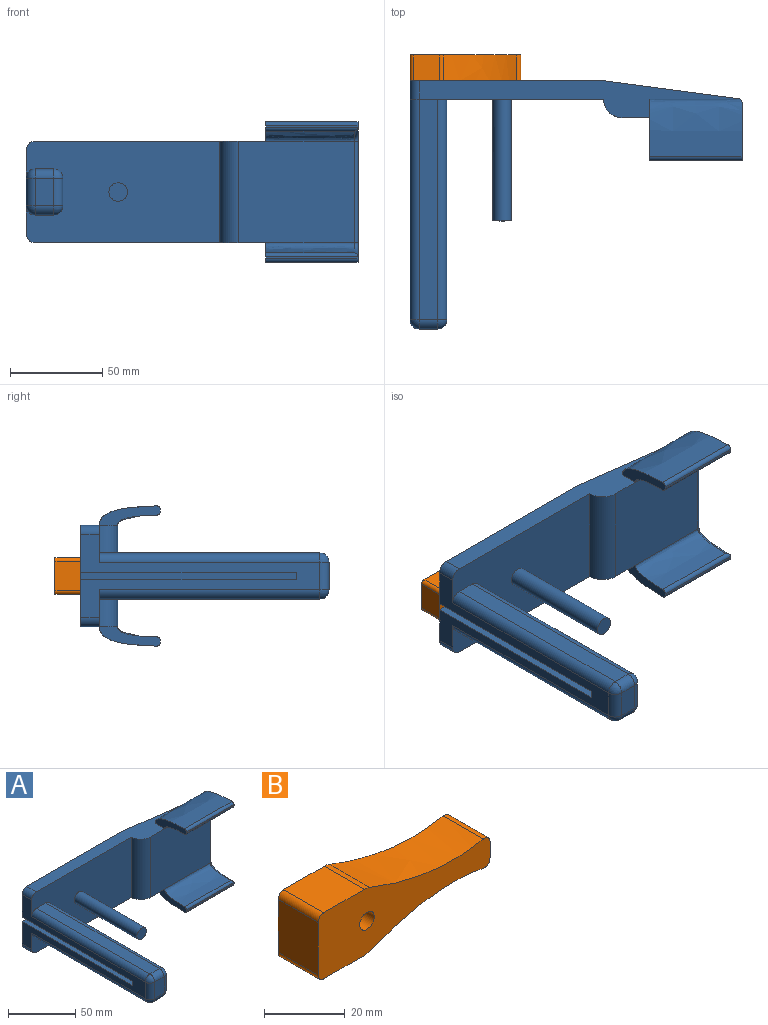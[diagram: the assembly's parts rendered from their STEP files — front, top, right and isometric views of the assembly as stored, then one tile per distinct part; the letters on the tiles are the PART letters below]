
ASSEMBLY  parts=2 mates=1
PART A: 53 faces, bbox 180x139.6x76.1 mm
  f0: plane 173.94x20mm, normal (0,0,1), area 1603.2mm2, adj f3,f15,f19,f21,f26,f28,f30,f32
  f1: plane 119.58x9.96mm, normal (0,0,-1), area 1191mm2, adj f15,f35,f40,f41
  f2: plane 119.58x9.96mm, normal (0,0,1), area 1191mm2, adj f15,f33,f38,f39
  f3: plane 104.98x55mm, normal (0,1,0), area 5710.5mm2, adj f0,f5,f7,f9,f10,f11,f12,f13
  f4: plane 119.58x15mm, normal (1,0,0), area 1793.7mm2, adj f15,f33,f34,f35
  f5: plane 129.58x45mm, normal (-1,0,0), area 1776.5mm2, adj f3,f9,f13,f14,f15,f31,f32,f38
  f6: plane 15x9.96mm, normal (0,-1,0), area 149.4mm2, adj f34,f39,f40,f44
  f7: cylinder r=2.5mm len=5mm, axis (0,-1,0), area 78.5mm2, adj f3,f8
  f8: plane 5x5mm, normal (0,1,0), area 19.6mm2, adj f7
  f9: plane 116.8x5mm, normal (0,0,-1), area 584mm2, adj f3,f5,f10,f14
  f10: plane 116.8x2.12mm, normal (0.71,0,-0.71), area 350.4mm2, adj f3,f9,f11,f14
  f11: plane 116.8x8.24mm, normal (-1,0,0), area 962.7mm2, adj f3,f10,f12,f14
  f12: plane 116.8x2.12mm, normal (0.71,0,0.71), area 350.4mm2, adj f3,f11,f13,f14
  f13: plane 116.8x5mm, normal (0,0,1), area 584mm2, adj f3,f5,f12,f14
  f14: plane 8.24x7.12mm, normal (0,1,0), area 33mm2, adj f5,f9,f10,f11,f12,f13
  f15: plane 104.98x55mm, normal (0,-1,0), area 5207mm2, adj f0,f1,f2,f4,f5,f16,f18,f30
  f16: cylinder r=5mm len=66mm, axis (0,1,0), area 2073.5mm2, adj f15,f17
  f17: plane 10x10mm, normal (0,-1,0), area 78.5mm2, adj f16
  f18: plane 173.94x20mm, normal (0,0,-1), area 1603.2mm2, adj f3,f15,f19,f21,f23,f24,f30,f31
  f19: plane 63x55mm, normal (0,-1,0), area 3465mm2, adj f0,f18,f25,f27,f30,f47
  f20: plane 76.06x33.12mm, normal (1,0,0), area 594.8mm2, adj f22,f24,f28,f29,f46,f47,f49,f50
  f21: plane 73.26x55mm, normal (0.13,0.99,0), area 4065.2mm2, adj f0,f3,f18,f52
  f22: plane 50x1.01mm, normal (0,-1,0), area 50.4mm2, adj f20,f23,f48,f49,f51
  f23: plane 33.11x10.53mm, normal (-1,0,0), area 183mm2, adj f18,f22,f24,f25,f48,f51
  f24: extruded ~50x31.09mm, area 1763.7mm2, adj f18,f20,f23,f51,f52
  f25: extruded ~48x21.14mm, area 1106.2mm2, adj f19,f23,f48,f49
  f26: plane 33.11x10.53mm, normal (-1,0,0), area 183mm2, adj f0,f27,f28,f29,f45,f50
  f27: extruded ~48x21.14mm, area 1106.2mm2, adj f19,f26,f45,f46
  f28: extruded ~50x31.09mm, area 1763.7mm2, adj f0,f20,f26,f50,f52
  f29: plane 50x1.01mm, normal (0,-1,0), area 50.4mm2, adj f20,f26,f45,f46,f50
  f30: cylinder r=10mm len=55mm, axis (0,0,-1), area 863.9mm2, adj f0,f15,f18,f19
  f31: cylinder r=5mm len=10mm, axis (0,-1,0), area 78.5mm2, adj f3,f5,f15,f18
  f32: cylinder r=5mm len=10mm, axis (0,-1,0), area 78.5mm2, adj f0,f3,f5,f15
  f33: cylinder r=5mm len=119.58mm, axis (0,-1,0), area 939.2mm2, adj f2,f4,f15,f36
  f34: cylinder r=5mm len=15mm, axis (0,0,1), area 117.8mm2, adj f4,f6,f36,f37
  f35: cylinder r=5mm len=119.58mm, axis (0,1,0), area 939.2mm2, adj f1,f4,f15,f37
  f36: sphere r=5mm, area 39.3mm2, adj f33,f34,f39
  f37: sphere r=5mm, area 39.3mm2, adj f34,f35,f40
  f38: cylinder r=5mm len=119.58mm, axis (0,1,0), area 939.2mm2, adj f2,f5,f15,f42
  f39: cylinder r=5mm len=9.96mm, axis (-1,0,0), area 78.2mm2, adj f2,f6,f36,f42
  f40: cylinder r=5mm len=9.96mm, axis (1,0,0), area 78.2mm2, adj f1,f6,f37,f43
  f41: cylinder r=5mm len=119.58mm, axis (0,-1,0), area 939.2mm2, adj f1,f5,f15,f43
  f42: sphere r=5mm, area 39.3mm2, adj f38,f39,f44
  f43: sphere r=5mm, area 39.3mm2, adj f40,f41,f44
  f44: cylinder r=5mm len=15mm, axis (0,0,-1), area 117.8mm2, adj f5,f6,f42,f43
  f45: cylinder r=2mm len=50mm, axis (1,0,0), area 152.5mm2, adj f26,f27,f29,f46
  f46: bspline ~26.24x10.11mm, area 79.9mm2, adj f20,f27,f29,f45,f47
  f47: cylinder r=2mm len=55mm, axis (0,0,-1), area 172.8mm2, adj f19,f20,f46,f49
  f48: cylinder r=2mm len=50mm, axis (1,0,0), area 152.5mm2, adj f22,f23,f25,f49
  f49: bspline ~26.24x10.11mm, area 79.9mm2, adj f20,f22,f25,f47,f48
  f50: cylinder r=2mm len=50mm, axis (1,0,0), area 158.1mm2, adj f20,f26,f28,f29
  f51: cylinder r=2mm len=50mm, axis (1,0,0), area 158.1mm2, adj f20,f22,f23,f24
  f52: cylinder r=2mm len=63.57mm, axis (0,0,1), area 169.9mm2, adj f0,f18,f20,f21,f24,f28
PART B: 16 faces, bbox 60.1x14x20 mm
  f0: plane 60.09x20mm, normal (0,1,0), area 776.8mm2, adj f2,f3,f4,f7,f8,f9,f10,f11
  f1: plane 60.09x20mm, normal (0,-1,0), area 756.4mm2, adj f2,f3,f4,f5,f7,f8,f9,f10
  f2: plane 14x4.92mm, normal (1,0,0), area 68.9mm2, adj f0,f1,f9,f10
  f3: plane 14.11x14mm, normal (0,0,1), area 197.6mm2, adj f0,f1,f12,f15
  f4: plane 14.11x14mm, normal (0,0,-1), area 197.6mm2, adj f0,f1,f13,f14
  f5: cylinder r=2.55mm len=5.1mm, axis (0,-1,0), area 80.1mm2, adj f1,f6
  f6: plane 5.1x5.1mm, normal (0,-1,0), area 20.4mm2, adj f5
  f7: extruded ~39.7x14mm, area 568.8mm2, adj f0,f1,f10,f15
  f8: extruded ~39.7x14mm, area 568.8mm2, adj f0,f1,f9,f14
  f9: cylinder r=2mm len=14mm, axis (0,1,0), area 49.9mm2, adj f0,f1,f2,f8
  f10: cylinder r=2mm len=14mm, axis (0,1,0), area 49.9mm2, adj f0,f1,f2,f7
  f11: plane 16x14mm, normal (-1,0,0), area 224mm2, adj f0,f1,f12,f13
  f12: cylinder r=2mm len=14mm, axis (0,1,0), area 44mm2, adj f0,f1,f3,f11
  f13: cylinder r=2mm len=14mm, axis (0,-1,0), area 44mm2, adj f0,f1,f4,f11
  f14: cylinder r=5mm len=14mm, axis (0,1,0), area 26.6mm2, adj f0,f1,f4,f8
  f15: cylinder r=5mm len=14mm, axis (0,1,0), area 26.6mm2, adj f0,f1,f3,f7
PLACE A t=(31.49,9.83,-18.59)mm
PLACE B t=(-4.38,77.05,71.51)mm
MATE revolute B.f5 <-> A.f7  axis (0,-1,0) through (5.62,77.05,-18.59)mm
